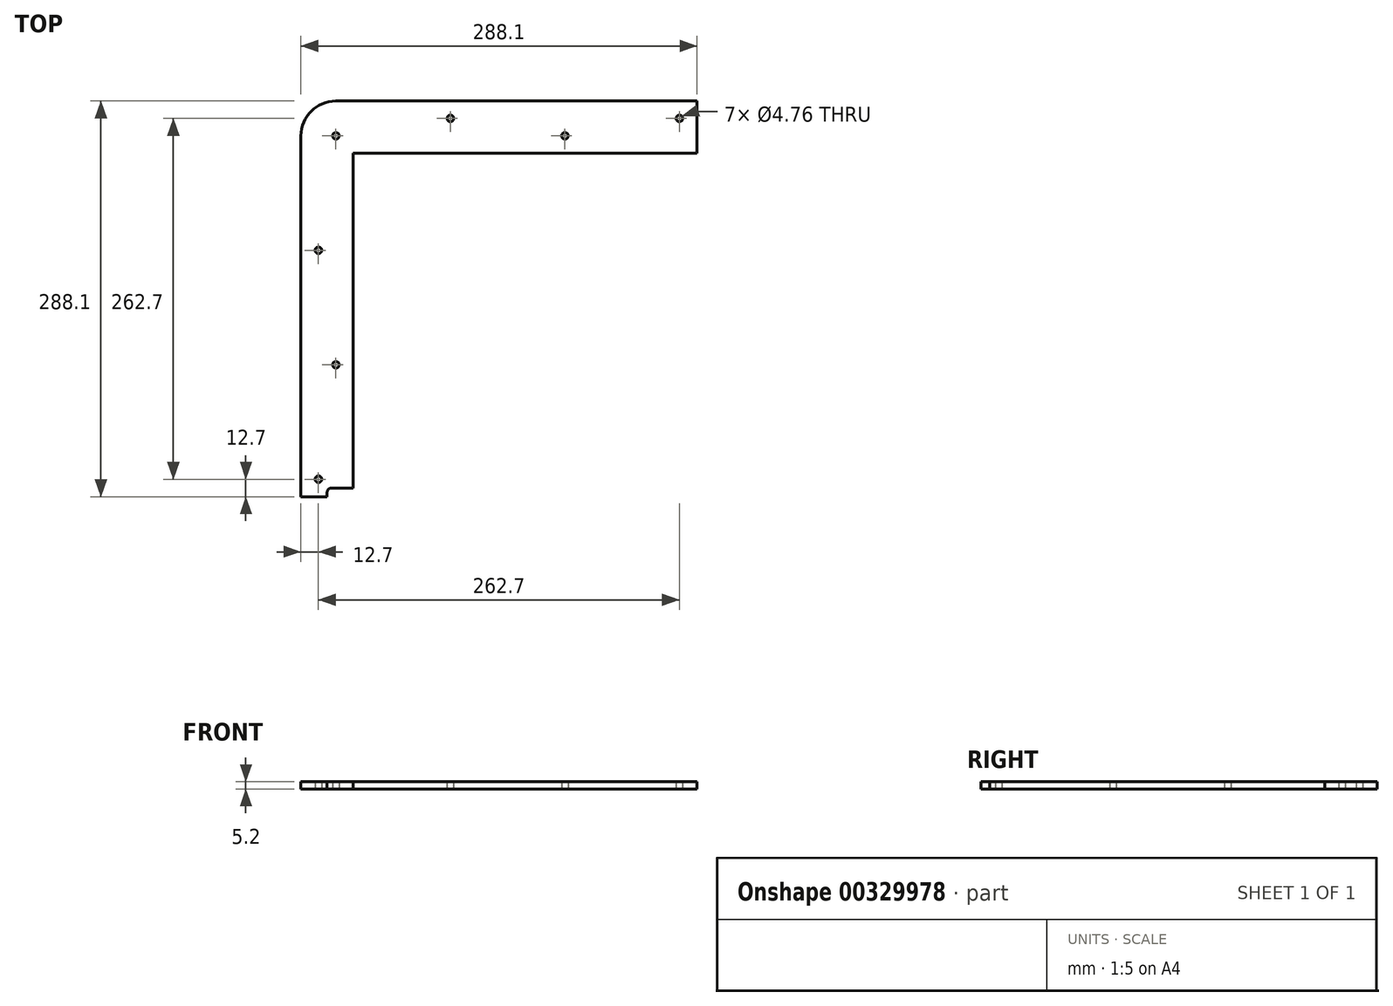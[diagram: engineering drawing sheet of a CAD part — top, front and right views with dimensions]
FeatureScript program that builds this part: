
annotation { "Feature Type Name" : "Feature", "Feature Type Description" : "" }
export const myFeature = defineFeature(function(context is Context, id is Id, definition is map)
    precondition{}
    {
        {
            var Q0;
            Q0=qCreatedBy(makeId("Top.planeOp"),FACE);
            var sketch = newSketch(context, id + "F0", { "sketchPlane" : qUnion([Q0])});
            skLineSegment(sketch, "E0.bottom", {"start": v(250, -250) * mm, "end": v(-250, -250) * mm, "construction": true});
            skLineSegment(sketch, "E0.top", {"start": v(250, 250) * mm, "end": v(-250, 250) * mm, "construction": true});
            skLineSegment(sketch, "E0.left", {"start": v(250, -250) * mm, "end": v(250, 250) * mm, "construction": true});
            skLineSegment(sketch, "E0.right", {"start": v(-250, -250) * mm, "end": v(-250, 250) * mm, "construction": true});
            skPoint(sketch, "E0.middle", {"position": v(0, 0) * mm});
            skSolve(sketch);
        }
        {
            var Q0;
            Q0=qCreatedBy(makeId("Top.planeOp"),FACE);
            var sketch = newSketch(context, id + "F1", { "sketchPlane" : qUnion([Q0])});
            skLineSegment(sketch, "E1", {"start": v(0, 0) * mm, "end": v(0, 250) * mm, "construction": true});
            skLineSegment(sketch, "E2", {"start": v(-250, 250) * mm, "end": v(0, 250) * mm});
            skLineSegment(sketch, "E3", {"start": v(0, 250) * mm, "end": v(0, 288.1) * mm});
            skLineSegment(sketch, "E4", {"start": v(0, 288.1) * mm, "end": v(-262.7, 288.1) * mm});
            skLineSegment(sketch, "E5", {"start": v(-288.1, 262.7) * mm, "end": v(-288.1, 0) * mm});
            skLineSegment(sketch, "E6", {"start": v(-250, 6.35) * mm, "end": v(-250, 250) * mm});
            skLineSegment(sketch, "E7", {"start": v(0, 0) * mm, "end": v(-250, 0) * mm, "construction": true});
            skLineSegment(sketch, "E8", {"start": v(-250, 6.35) * mm, "end": v(-250, 0) * mm, "construction": true});
            skPoint(sketch, "E9.visualSharp", {"position": v(-288.1, 288.1) * mm});
            skArc(sketch, "E9.filletArc", {"start": v(-262.7, 288.1) * mm, "mid": v(-280.66, 280.66) * mm, "end": v(-288.1, 262.7) * mm});
            skLineSegment(sketch, "E10", {"start": v(-288.1, 288.1) * mm, "end": v(0, 0) * mm, "construction": true});
            skLineSegment(sketch, "E11.bottom", {"start": v(-262.7, 262.7) * mm, "end": v(-275.4, 262.7) * mm, "construction": true});
            skLineSegment(sketch, "E11.top", {"start": v(-262.7, 12.7) * mm, "end": v(-275.4, 12.7) * mm, "construction": true});
            skLineSegment(sketch, "E11.left", {"start": v(-262.7, 262.7) * mm, "end": v(-262.7, 12.7) * mm, "construction": true});
            skLineSegment(sketch, "E11.right", {"start": v(-275.4, 262.7) * mm, "end": v(-275.4, 12.7) * mm, "construction": true});
            skPoint(sketch, "E11.middle", {"position": v(-269.05, 137.7) * mm});
            skLineSegment(sketch, "E12", {"start": v(-288.1, 0) * mm, "end": v(-275.4, 12.7) * mm, "construction": true});
            skLineSegment(sketch, "E13", {"start": v(-250, 6.35) * mm, "end": v(-265.88, 6.35) * mm});
            skArc(sketch, "E14.filletArc", {"start": v(-265.88, 6.35) * mm, "mid": v(-268.12, 5.42) * mm, "end": v(-269.05, 3.18) * mm});
            skLineSegment(sketch, "E15", {"start": v(-288.1, 0) * mm, "end": v(-269.05, 0) * mm});
            skLineSegment(sketch, "E16", {"start": v(-269.05, 0) * mm, "end": v(-269.05, 3.18) * mm});
            skLineSegment(sketch, "E17", {"start": v(-269.05, 0) * mm, "end": v(-250, 0) * mm, "construction": true});
            skCircle(sketch, "E18", {"center": v(-275.4, 12.7) * mm, "radius": 2.38 * mm});
            skCircle(sketch, "E19", {"center": v(-262.7, 262.7) * mm, "radius": 2.38 * mm});
            skCircle(sketch, "E20", {"center": v(-262.7, 96.03) * mm, "radius": 2.38 * mm});
            skCircle(sketch, "E21", {"center": v(-275.4, 179.37) * mm, "radius": 2.38 * mm});
            skLineSegment(sketch, "E22", {"start": v(-262.7, 96.03) * mm, "end": v(-275.4, 179.37) * mm, "construction": true});
            skLineSegment(sketch, "E23", {"start": v(-275.4, 179.37) * mm, "end": v(-262.7, 262.7) * mm, "construction": true});
            skCircle(sketch, "E24.MirrorC", {"center": v(-179.37, 275.4) * mm, "radius": 2.38 * mm});
            skCircle(sketch, "E25.MirrorC", {"center": v(-96.03, 262.7) * mm, "radius": 2.38 * mm});
            skCircle(sketch, "E26.MirrorC", {"center": v(-12.7, 275.4) * mm, "radius": 2.38 * mm});
            skLineSegment(sketch, "E27", {"start": v(-262.7, 12.7) * mm, "end": v(-250, 12.7) * mm, "construction": true});
            skLineSegment(sketch, "E28", {"start": v(-275.4, 12.7) * mm, "end": v(-288.1, 12.7) * mm, "construction": true});
            skLineSegment(sketch, "E29", {"start": v(-262.7, 96.03) * mm, "end": v(-275.4, 12.7) * mm, "construction": true});
            skSolve(sketch);
        }
        {
            var Q0;
            Q0 = qSketchRegion(id + "F1", true);
            extrude(context, id + "F2", {"entities" : qUnion([Q0]), "depth" : 5.2 * mm});
        }
    });
